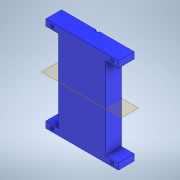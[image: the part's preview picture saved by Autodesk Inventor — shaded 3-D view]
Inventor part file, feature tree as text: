
AUTODESK INVENTOR PART (.ipt)
format: ipt  version: 2020 (Build 240168000, 168)  size: 156,672 bytes
history: native  units: mm
features: extrude x4, sketch x4, plane x2, mirror x2
ambient origin geometry x8: Origin, YZ Plane, XZ Plane, XY Plane, X Axis, Y Axis, Z Axis, Center Point
bodies: Solid1 (feature_tree)
feature tree (12):
  extrude  "Extrusion1"  Depth=600.0mm
  extrude  "Extrusion2"  Depth=80.0mm
  extrude  "Extrusion3"  Depth=100.0mm TaperAngle=0.0deg
  plane  "Work Plane1"
  mirror  "Mirror1"
  plane  "Work Plane2"
  mirror  "Mirror2"
  extrude  "Extrusion4"  Depth=18.3mm
  sketch  "Sketch1"  dims[d0=300.0mm d1=600.0mm]
  sketch  "Sketch2"  dims[d2=100.0mm d3=0.0mm d4=80.0mm]
  sketch  "Sketch3"  dims[d5=40.0mm d6=100.0mm d7=0.0mm]
  sketch  "Sketch4"  dims[d8=24.0mm d9=18.3mm d10=100.0mm d11=0.0mm d12=20.0mm d13=15.0mm d14=0.0mm d15=0.0mm]
